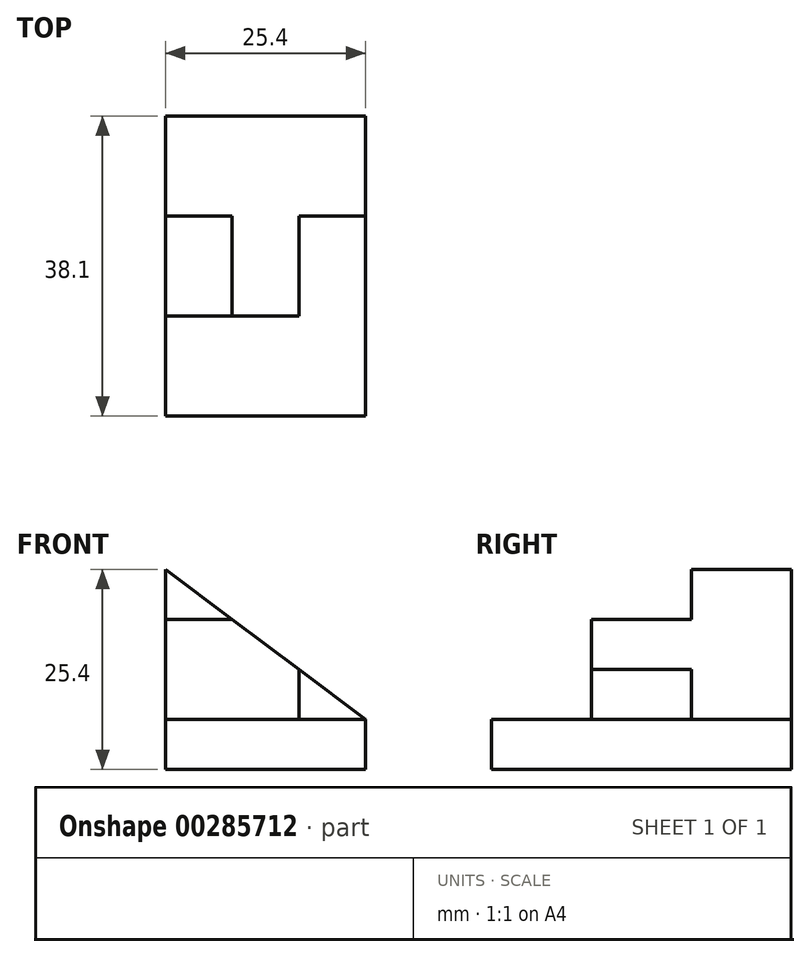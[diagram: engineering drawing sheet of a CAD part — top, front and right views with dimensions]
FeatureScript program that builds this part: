
annotation { "Feature Type Name" : "Feature", "Feature Type Description" : "" }
export const myFeature = defineFeature(function(context is Context, id is Id, definition is map)
    precondition{}
    {
        {
            var Q0;
            Q0=qCreatedBy(makeId("Front.planeOp"),FACE);
            var sketch = newSketch(context, id + "F0", { "sketchPlane" : qUnion([Q0])});
            skLineSegment(sketch, "E0.bottom", {"start": v(0, 0) * mm, "end": v(25.4, 0) * mm});
            skLineSegment(sketch, "E0.top", {"start": v(0, 6.35) * mm, "end": v(25.4, 6.35) * mm});
            skLineSegment(sketch, "E0.left", {"start": v(0, 0) * mm, "end": v(0, 6.35) * mm});
            skLineSegment(sketch, "E0.right", {"start": v(25.4, 0) * mm, "end": v(25.4, 6.35) * mm});
            skSolve(sketch);
        }
        {
            var Q0;
            Q0 = qSketchRegion(id + "F0", true);
            extrude(context, id + "F1", {"entities" : qUnion([Q0]), "depth" : 38.1 * mm});
        }
        {
            var Q0;
            Q0=qCreatedBy(makeId("Front.planeOp"),FACE);
            var sketch = newSketch(context, id + "F2", { "sketchPlane" : qUnion([Q0])});
            skLineSegment(sketch, "E1", {"start": v(16.93, 6.35) * mm, "end": v(16.93, 12.7) * mm});
            skLineSegment(sketch, "E2", {"start": v(16.93, 12.7) * mm, "end": v(8.47, 19.05) * mm});
            skLineSegment(sketch, "E3", {"start": v(8.47, 19.05) * mm, "end": v(0, 19.05) * mm});
            skLineSegment(sketch, "E4", {"start": v(0, 19.05) * mm, "end": v(0, 6.35) * mm});
            skLineSegment(sketch, "E5", {"start": v(0, 25.4) * mm, "end": v(25.4, 6.35) * mm, "construction": true});
            skLineSegment(sketch, "E6", {"start": v(16.93, 6.35) * mm, "end": v(0, 6.35) * mm});
            skSolve(sketch);
        }
        {
            var Q0;
            Q0 = qSketchRegion(id + "F2", true);
            extrude(context, id + "F3", {"entities" : qUnion([Q0]), "operationType" : NewBodyOperationType.ADD, "depth" : 25.4 * mm});
        }
        {
            var Q0;
            Q0=qCreatedBy(makeId("Front.planeOp"),FACE);
            var sketch = newSketch(context, id + "F4", { "sketchPlane" : qUnion([Q0])});
            skLineSegment(sketch, "E7", {"start": v(25.4, 6.35) * mm, "end": v(0, 25.4) * mm});
            skLineSegment(sketch, "E8", {"start": v(25.4, 6.35) * mm, "end": v(16.93, 6.35) * mm});
            skLineSegment(sketch, "E9", {"start": v(16.93, 6.35) * mm, "end": v(16.93, 12.7) * mm});
            skLineSegment(sketch, "E10", {"start": v(8.47, 19.05) * mm, "end": v(0, 19.05) * mm});
            skLineSegment(sketch, "E11", {"start": v(0, 19.05) * mm, "end": v(0, 25.4) * mm});
            skSolve(sketch);
        }
        {
            var Q0;
            Q0 = qSketchRegion(id + "F4", true);
            extrude(context, id + "F5", {"entities" : qUnion([Q0]), "operationType" : NewBodyOperationType.ADD, "depth" : 12.7 * mm});
        }
    });
